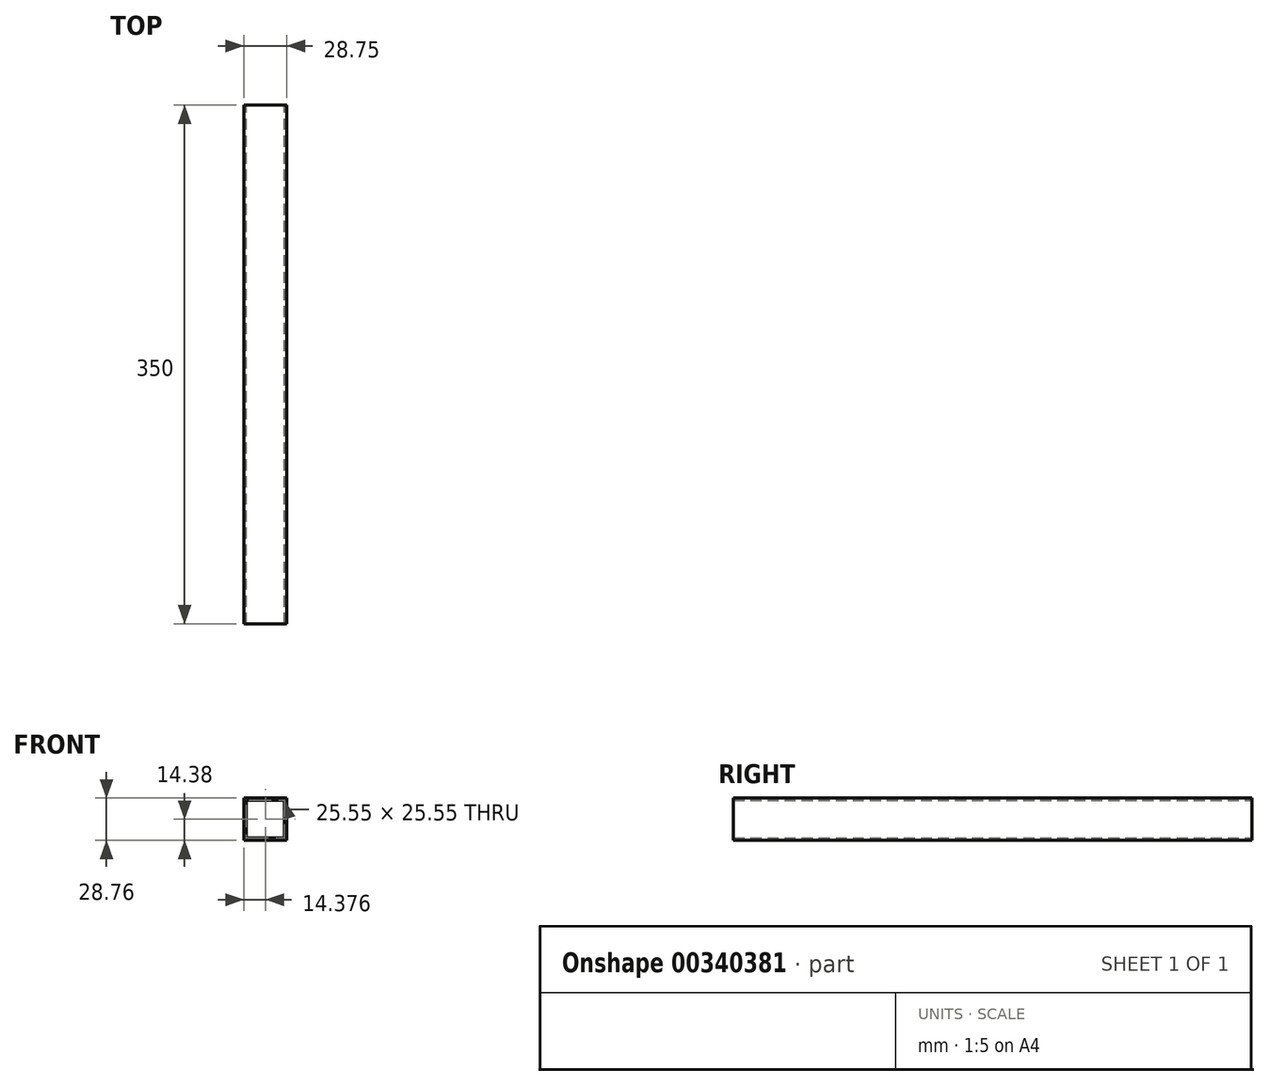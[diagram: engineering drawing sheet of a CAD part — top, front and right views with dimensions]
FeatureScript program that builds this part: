
annotation { "Feature Type Name" : "Feature", "Feature Type Description" : "" }
export const myFeature = defineFeature(function(context is Context, id is Id, definition is map)
    precondition{}
    {
        {
            var Q0;
            Q0=qCreatedBy(makeId("Front.planeOp"),FACE);
            var sketch = newSketch(context, id + "F0", { "sketchPlane" : qUnion([Q0])});
            skLineSegment(sketch, "E0.bottom", {"start": v(12.32, 14.38) * mm, "end": v(-16.43, 14.38) * mm});
            skLineSegment(sketch, "E0.top", {"start": v(12.32, -14.38) * mm, "end": v(-16.43, -14.38) * mm});
            skLineSegment(sketch, "E0.left", {"start": v(12.32, 14.37) * mm, "end": v(12.32, -14.38) * mm});
            skLineSegment(sketch, "E0.right", {"start": v(-16.43, 14.38) * mm, "end": v(-16.43, -14.38) * mm});
            skPoint(sketch, "E0.middle", {"position": v(-2.05, 0) * mm});
            skSolve(sketch);
        }
        {
            var Q0;
            Q0=makeQuery(id+"F0.imprint","IMPRINT",FACE,{"disambiguationData":[TD([[makeQuery(id+"F0.imprint","IMPRINT",EDGE,{"derivedFrom":sQuery(id+"F0.wireOp",EDGE,"E0.bottom")}),1.0]])]});
            extrude(context, id + "F1", {"entities" : qUnion([Q0]), "depth" : 350 * mm});
        }
        {
            var Q0;
            Q0=makeQuery(id+"F1.opExtrude","CAP_FACE",FACE,{"disambiguationData":[OSD([sQuery(id+"F0.wireOp",EDGE,"E0.bottom"),sQuery(id+"F0.wireOp",EDGE,"E0.top"),sQuery(id+"F0.wireOp",EDGE,"E0.left"),sQuery(id+"F0.wireOp",EDGE,"E0.right")])],"isStart":false});
            var Q1;
            Q1=makeQuery(id+"F1.opExtrude","CAP_FACE",FACE,{"disambiguationData":[OSD([sQuery(id+"F0.wireOp",EDGE,"E0.bottom"),sQuery(id+"F0.wireOp",EDGE,"E0.top"),sQuery(id+"F0.wireOp",EDGE,"E0.left"),sQuery(id+"F0.wireOp",EDGE,"E0.right")])],"isStart":true});
            shell(context, id + "F2", {"entities" : qUnion([Q0, Q1]), "thickness" : 1.6 * mm});
        }
    });
